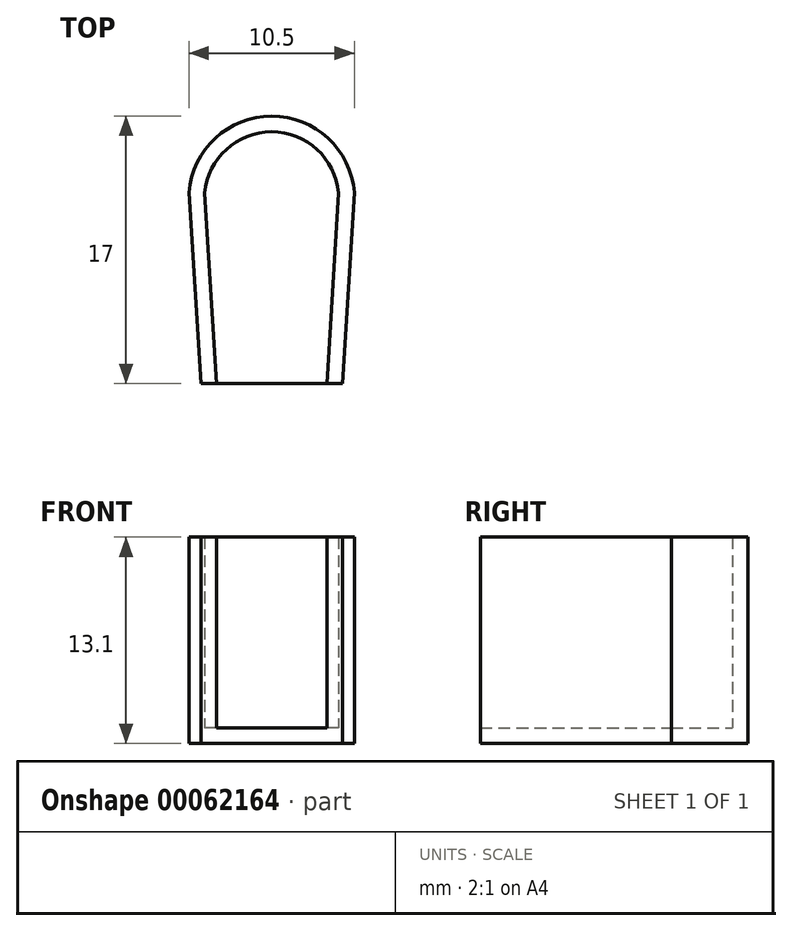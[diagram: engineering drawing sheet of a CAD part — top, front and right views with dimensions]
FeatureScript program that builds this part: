
annotation { "Feature Type Name" : "Feature", "Feature Type Description" : "" }
export const myFeature = defineFeature(function(context is Context, id is Id, definition is map)
    precondition{}
    {
        {
            var Q0;
            Q0=qCreatedBy(makeId("Top.planeOp"),FACE);
            var sketch = newSketch(context, id + "F0", { "sketchPlane" : qUnion([Q0])});
            skLineSegment(sketch, "E0", {"start": v(-3.5, 0) * mm, "end": v(3.5, 0) * mm});
            skLineSegment(sketch, "E1", {"start": v(-3.5, 0) * mm, "end": v(-4.25, 12.12) * mm});
            skLineSegment(sketch, "E2", {"start": v(4.25, 12.12) * mm, "end": v(3.5, 0) * mm});
            skPoint(sketch, "E3", {"position": v(-4.25, 12.12) * mm});
            skPoint(sketch, "E4", {"position": v(4.25, 12.12) * mm});
            skArc(sketch, "E5", {"start": v(4.25, 12.12) * mm, "mid": v(0, 16) * mm, "end": v(-4.25, 12.12) * mm});
            skLineSegment(sketch, "E6", {"start": v(0, 16) * mm, "end": v(0, 0) * mm, "construction": true});
            skLineSegment(sketch, "E7", {"start": v(-4.25, 12.12) * mm, "end": v(4.25, 12.12) * mm, "construction": true});
            skSolve(sketch);
        }
        {
            var Q0;
            Q0 = qSketchRegion(id + "F0", true);
            extrude(context, id + "F1", {"entities" : qUnion([Q0]), "depth" : 12.1 * mm});
        }
        {
            var Q0;
            Q0=makeQuery(id+"F1.opExtrude","CAP_FACE",FACE,{"disambiguationData":[OSD([sQuery(id+"F0.wireOp",EDGE,"E0"),sQuery(id+"F0.wireOp",EDGE,"E1"),sQuery(id+"F0.wireOp",EDGE,"E2"),sQuery(id+"F0.wireOp",EDGE,"E5")])],"isStart":false});
            shell(context, id + "F2", {"entities" : qUnion([Q0]), "thickness" : 1 * mm, "oppositeDirection" : true});
        }
        {
            var Q0;
            Q0=makeQuery(id+"F2.opShell","OFFSET_FACE",FACE,{"disambiguationData":[OSD([sQuery(id+"F0.wireOp",EDGE,"E0")])]});
            var sketch = newSketch(context, id + "F3", { "sketchPlane" : qUnion([Q0])});
            skLineSegment(sketch, "E8.bottom", {"start": v(6.76, -1.3) * mm, "end": v(-7.2, -1.3) * mm});
            skLineSegment(sketch, "E8.top", {"start": v(6.76, 12.71) * mm, "end": v(-7.2, 12.71) * mm});
            skLineSegment(sketch, "E8.left", {"start": v(6.76, -1.3) * mm, "end": v(6.76, 12.71) * mm});
            skLineSegment(sketch, "E8.right", {"start": v(-7.2, -1.3) * mm, "end": v(-7.2, 12.71) * mm});
            skSolve(sketch);
        }
        {
            var Q0;
            Q0 = qSketchRegion(id + "F3", true);
            extrude(context, id + "F4", {"entities" : qUnion([Q0]), "operationType" : NewBodyOperationType.REMOVE, "oppositeDirection" : true, "depth" : 25 * mm});
        }
    });
